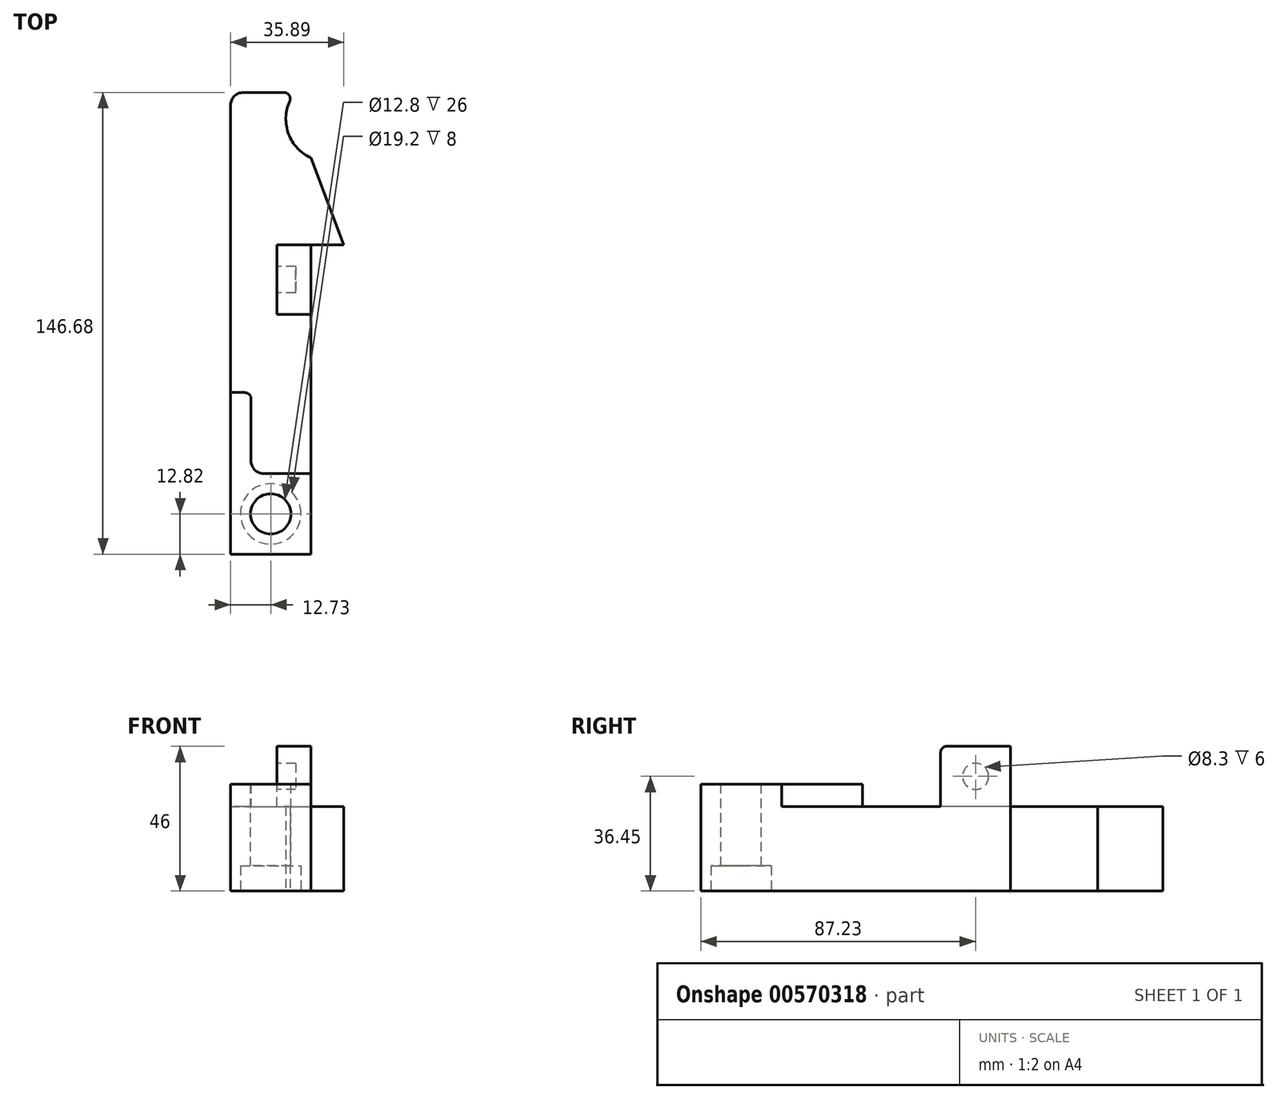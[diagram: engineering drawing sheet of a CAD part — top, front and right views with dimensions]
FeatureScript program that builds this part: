
annotation { "Feature Type Name" : "Feature", "Feature Type Description" : "" }
export const myFeature = defineFeature(function(context is Context, id is Id, definition is map)
    precondition{}
    {
        {
            var Q0;
            Q0=qCreatedBy(makeId("Top.planeOp"),FACE);
            var sketch = newSketch(context, id + "F0", { "sketchPlane" : qUnion([Q0])});
            skLineSegment(sketch, "E0.bottom", {"start": v(-25.46, 73.34) * mm, "end": v(-4.96, 73.34) * mm});
            skLineSegment(sketch, "E0.top", {"start": v(-25.46, -73.34) * mm, "end": v(0, -73.34) * mm});
            skLineSegment(sketch, "E0.left", {"start": v(-25.46, 69.34) * mm, "end": v(-25.46, -73.34) * mm});
            skLineSegment(sketch, "E0.right", {"start": v(0, 73.34) * mm, "end": v(0, -73.34) * mm});
            skLineSegment(sketch, "E1", {"start": v(0, 73.34) * mm, "end": v(0, 25) * mm, "construction": true});
            skLineSegment(sketch, "E2", {"start": v(0, 25) * mm, "end": v(10.43, 25) * mm});
            skLineSegment(sketch, "E3", {"start": v(10.43, 25) * mm, "end": v(0, 52.61) * mm});
            skLineSegment(sketch, "E4", {"start": v(0, 52.61) * mm, "end": v(0, 25) * mm, "construction": true});
            skLineSegment(sketch, "E5", {"start": v(-21.46, 73.34) * mm, "end": v(-8.52, 73.34) * mm, "construction": true});
            skLineSegment(sketch, "E6", {"start": v(-4.96, 73.34) * mm, "end": v(0, 73.34) * mm, "construction": true});
            skArc(sketch, "E7", {"start": v(-6.7, 70.5) * mm, "mid": v(-7.06, 60.17) * mm, "end": v(0, 52.61) * mm});
            skPoint(sketch, "E8.visualSharp", {"position": v(-25.46, 73.34) * mm});
            skArc(sketch, "E8.filletArc", {"start": v(-21.46, 73.34) * mm, "mid": v(-24.29, 72.17) * mm, "end": v(-25.46, 69.34) * mm});
            skPoint(sketch, "E9.visualSharp", {"position": v(-4.96, 73.34) * mm});
            skArc(sketch, "E9.filletArc", {"start": v(-6.7, 70.5) * mm, "mid": v(-6.84, 72.42) * mm, "end": v(-8.52, 73.34) * mm});
            skSolve(sketch);
        }
        {
            var Q0;
            {var subQ0=sQuery(id+"F0.wireOp",EDGE,"E2");Q0=makeQuery(id+"F0.imprint","IMPRINT",FACE,{"disambiguationData":[TD([[makeQuery(id+"F0.imprint","IMPRINT",EDGE,{"derivedFrom":subQ0}),1.0]])]});}
            var Q1;
            Q1=makeQuery(id+"F0.imprint","IMPRINT",FACE,{"disambiguationData":[TD([[makeQuery(id+"F0.imprint","IMPRINT",EDGE,{"derivedFrom":sQuery(id+"F0.wireOp",EDGE,"E0.bottom")}),-1.0]])]});
            extrude(context, id + "F1", {"entities" : qUnion([Q0, Q1]), "depth" : 26.9 * mm, "offsetDistance" : 25 * mm});
        }
        {
            var Q0;
            Q0=makeQuery(id+"F1.opExtrude","CAP_FACE",FACE,{"disambiguationData":[OSD([sQuery(id+"F0.wireOp",EDGE,"E0.bottom"),sQuery(id+"F0.wireOp",EDGE,"E0.top"),sQuery(id+"F0.wireOp",EDGE,"E0.left"),sQuery(id+"F0.wireOp",EDGE,"E0.right"),sQuery(id+"F0.wireOp",EDGE,"E2"),sQuery(id+"F0.wireOp",EDGE,"E3"),sQuery(id+"F0.wireOp",EDGE,"E7")])],"isStart":false});
            var sketch = newSketch(context, id + "F2", { "sketchPlane" : qUnion([Q0])});
            skLineSegment(sketch, "E10", {"start": v(0, -73.34) * mm, "end": v(-25.46, -73.34) * mm});
            skLineSegment(sketch, "E11", {"start": v(-25.46, -73.34) * mm, "end": v(-25.46, -21.98) * mm});
            skLineSegment(sketch, "E12", {"start": v(-25.46, -21.98) * mm, "end": v(-20.99, -21.98) * mm});
            skLineSegment(sketch, "E13", {"start": v(-18.99, -23.98) * mm, "end": v(-18.99, -43.7) * mm});
            skLineSegment(sketch, "E14", {"start": v(-14.99, -47.7) * mm, "end": v(0, -47.7) * mm});
            skLineSegment(sketch, "E15", {"start": v(0, -47.7) * mm, "end": v(0, -73.34) * mm});
            skPoint(sketch, "E16.visualSharp", {"position": v(-18.99, -21.98) * mm});
            skArc(sketch, "E16.filletArc", {"start": v(-18.99, -23.98) * mm, "mid": v(-19.58, -22.57) * mm, "end": v(-20.99, -21.98) * mm});
            skPoint(sketch, "E17.visualSharp", {"position": v(-18.99, -47.7) * mm});
            skArc(sketch, "E17.filletArc", {"start": v(-18.99, -43.7) * mm, "mid": v(-17.82, -46.53) * mm, "end": v(-14.99, -47.7) * mm});
            skSolve(sketch);
        }
        {
            var Q0;
            Q0=makeQuery(id+"F2.imprint","IMPRINT",FACE,{"disambiguationData":[TD([[makeQuery(id+"F2.imprint","IMPRINT",EDGE,{"derivedFrom":sQuery(id+"F2.wireOp",EDGE,"E10")}),1.0]])]});
            extrude(context, id + "F3", {"entities" : qUnion([Q0]), "operationType" : NewBodyOperationType.ADD, "depth" : 7.1 * mm, "offsetDistance" : 25 * mm});
        }
        {
            var Q0;
            Q0=makeQuery(id+"F3.boolean.opBoolean","MERGE",FACE,{"derivedFrom":[makeQuery(id+"F1.opExtrude","SWEPT_FACE",FACE,{"disambiguationData":[OSD([sQuery(id+"F0.wireOp",EDGE,"E0.right")])]}),makeQuery(id+"F3.opExtrude","SWEPT_FACE",FACE,{"disambiguationData":[OSD([sQuery(id+"F2.wireOp",EDGE,"E15")])]})]});
            var sketch = newSketch(context, id + "F4", { "sketchPlane" : qUnion([Q0])});
            skLineSegment(sketch, "E18.bottom", {"start": v(25, 26.9) * mm, "end": v(2.8, 26.9) * mm});
            skLineSegment(sketch, "E18.top", {"start": v(25, 46) * mm, "end": v(4.8, 46) * mm});
            skLineSegment(sketch, "E18.left", {"start": v(25, 26.9) * mm, "end": v(25, 46) * mm});
            skLineSegment(sketch, "E18.right", {"start": v(2.8, 26.9) * mm, "end": v(2.8, 44) * mm});
            skPoint(sketch, "E19.visualSharp", {"position": v(2.8, 46) * mm});
            skArc(sketch, "E19.filletArc", {"start": v(4.8, 46) * mm, "mid": v(3.38, 45.41) * mm, "end": v(2.8, 44) * mm});
            skSolve(sketch);
        }
        {
            var Q0;
            Q0=makeQuery(id+"F4.imprint","IMPRINT",FACE,{"disambiguationData":[TD([[makeQuery(id+"F4.imprint","IMPRINT",EDGE,{"derivedFrom":sQuery(id+"F4.wireOp",EDGE,"E18.bottom")}),-1.0]])]});
            extrude(context, id + "F5", {"entities" : qUnion([Q0]), "operationType" : NewBodyOperationType.ADD, "oppositeDirection" : true, "depth" : 10.8 * mm, "offsetDistance" : 25 * mm});
        }
        {
            var Q0;
            Q0=makeQuery(id+"F5.opExtrude","CAP_FACE",FACE,{"disambiguationData":[OSD([sQuery(id+"F4.wireOp",EDGE,"E18.bottom"),sQuery(id+"F4.wireOp",EDGE,"E18.top"),sQuery(id+"F4.wireOp",EDGE,"E18.left"),sQuery(id+"F4.wireOp",EDGE,"E18.right"),sQuery(id+"F4.wireOp",EDGE,"E19.filletArc")])],"isStart":false});
            var sketch = newSketch(context, id + "F6", { "sketchPlane" : qUnion([Q0])});
            skCircle(sketch, "E20", {"center": v(-13.9, 36.45) * mm, "radius": 4.15 * mm});
            skLineSegment(sketch, "E21", {"start": v(-25, 36.45) * mm, "end": v(-2.8, 36.45) * mm, "construction": true});
            skLineSegment(sketch, "E22", {"start": v(-13.9, 26.9) * mm, "end": v(-13.9, 46) * mm});
            skSolve(sketch);
        }
        {
            var Q0;
            Q0 = qSketchRegion(id + "F6", true);
            var Q1;
            Q1=sQuery(id+"F6.wireOp",EDGE,"E20");
            extrude(context, id + "F7", {"entities" : qUnion([Q0]), "operationType" : NewBodyOperationType.REMOVE, "surfaceEntities" : qUnion([Q1]), "oppositeDirection" : true, "depth" : 6 * mm, "offsetDistance" : 25 * mm});
        }
        {
            var Q0;
            Q0=makeQuery(id+"F3.opExtrude","CAP_FACE",FACE,{"disambiguationData":[OSD([sQuery(id+"F2.wireOp",EDGE,"E10"),sQuery(id+"F2.wireOp",EDGE,"E11"),sQuery(id+"F2.wireOp",EDGE,"E12"),sQuery(id+"F2.wireOp",EDGE,"E13"),sQuery(id+"F2.wireOp",EDGE,"E14"),sQuery(id+"F2.wireOp",EDGE,"E15"),sQuery(id+"F2.wireOp",EDGE,"E16.filletArc"),sQuery(id+"F2.wireOp",EDGE,"E17.filletArc")])],"isStart":false});
            var sketch = newSketch(context, id + "F8", { "sketchPlane" : qUnion([Q0])});
            skLineSegment(sketch, "E23", {"start": v(0, -60.52) * mm, "end": v(-25.46, -60.52) * mm, "construction": true});
            skLineSegment(sketch, "E24", {"start": v(-12.73, -73.34) * mm, "end": v(-12.73, -47.7) * mm, "construction": true});
            skCircle(sketch, "E25", {"center": v(-12.73, -60.52) * mm, "radius": 6.4 * mm});
            skSolve(sketch);
        }
        {
            var Q0;
            Q0 = qSketchRegion(id + "F8", true);
            extrude(context, id + "F9", {"entities" : qUnion([Q0]), "operationType" : NewBodyOperationType.REMOVE, "endBound" : BoundingType.THROUGH_ALL, "oppositeDirection" : true, "depth" : 25 * mm, "offsetDistance" : 25 * mm});
        }
        {
            var Q0;
            Q0=makeQuery(id+"F1.opExtrude","CAP_FACE",FACE,{"disambiguationData":[OSD([sQuery(id+"F0.wireOp",EDGE,"E0.bottom"),sQuery(id+"F0.wireOp",EDGE,"E0.top"),sQuery(id+"F0.wireOp",EDGE,"E0.left"),sQuery(id+"F0.wireOp",EDGE,"E0.right"),sQuery(id+"F0.wireOp",EDGE,"E2"),sQuery(id+"F0.wireOp",EDGE,"E3"),sQuery(id+"F0.wireOp",EDGE,"E7"),sQuery(id+"F0.wireOp",EDGE,"E8.filletArc"),sQuery(id+"F0.wireOp",EDGE,"E9.filletArc")])],"isStart":true});
            var sketch = newSketch(context, id + "F10", { "sketchPlane" : qUnion([Q0])});
            skCircle(sketch, "E26", {"center": v(-12.73, 60.52) * mm, "radius": 9.6 * mm});
            skSolve(sketch);
        }
        {
            var Q0;
            Q0=makeQuery(id+"F10.imprint","IMPRINT",FACE,{"disambiguationData":[TD([[makeQuery(id+"F10.imprint","IMPRINT",EDGE,{"derivedFrom":sQuery(id+"F10.wireOp",EDGE,"E26")}),1.0]])]});
            extrude(context, id + "F11", {"entities" : qUnion([Q0]), "operationType" : NewBodyOperationType.REMOVE, "oppositeDirection" : true, "depth" : 8 * mm, "offsetDistance" : 25 * mm});
        }
    });
